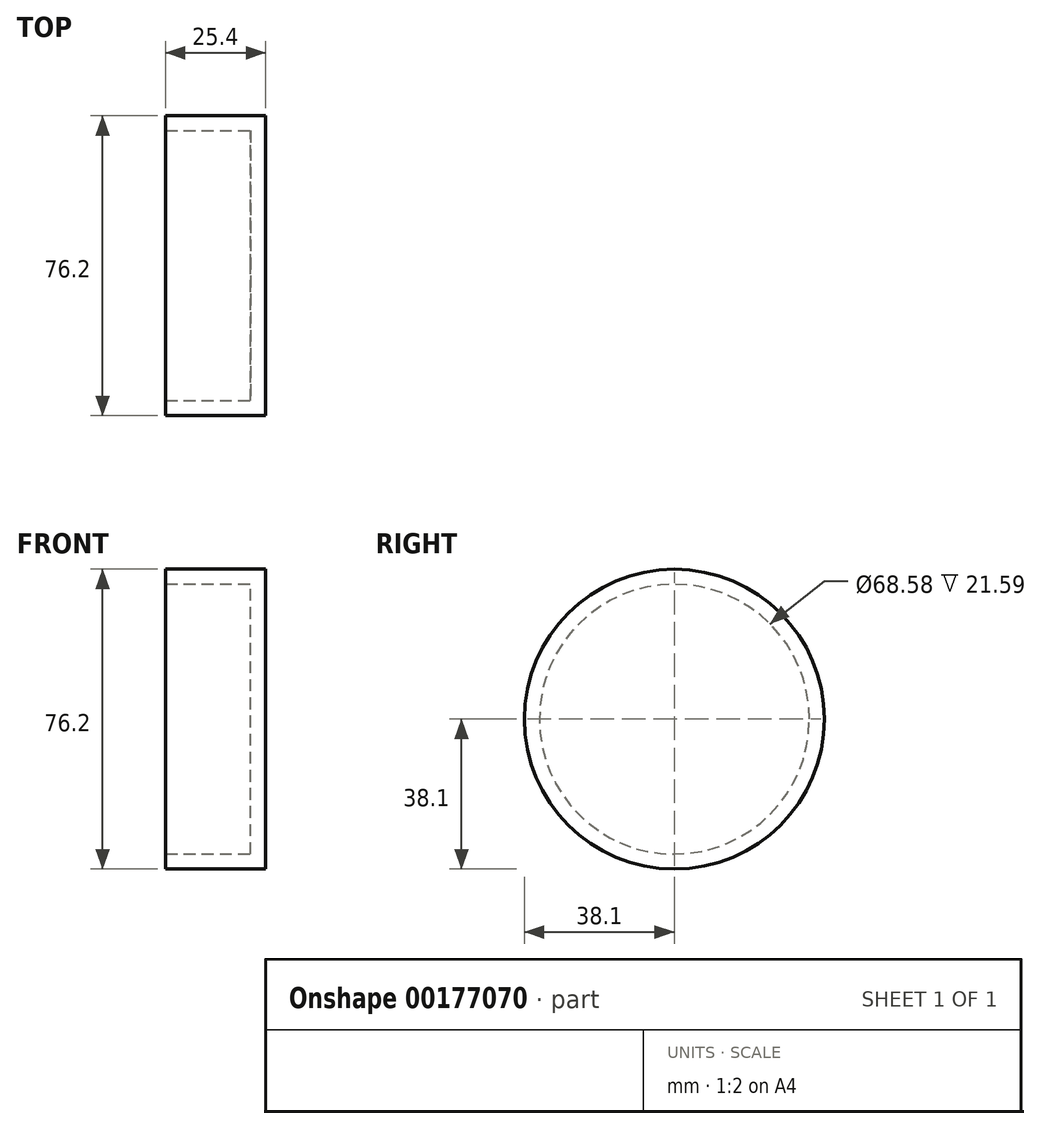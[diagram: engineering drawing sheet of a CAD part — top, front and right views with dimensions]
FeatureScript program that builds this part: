
annotation { "Feature Type Name" : "Feature", "Feature Type Description" : "" }
export const myFeature = defineFeature(function(context is Context, id is Id, definition is map)
    precondition{}
    {
        {
            var Q0;
            Q0=qCreatedBy(makeId("Right.planeOp"),FACE);
            var sketch = newSketch(context, id + "F0", { "sketchPlane" : qUnion([Q0])});
            skCircle(sketch, "E0", {"center": v(0, 0) * mm, "radius": 38.1 * mm});
            skSolve(sketch);
        }
        {
            var Q0;
            Q0=makeQuery(id+"F0.imprint","IMPRINT",FACE,{"disambiguationData":[TD([[makeQuery(id+"F0.imprint","IMPRINT",EDGE,{"derivedFrom":sQuery(id+"F0.wireOp",EDGE,"E0")}),1.0]])]});
            extrude(context, id + "F1", {"entities" : qUnion([Q0]), "oppositeDirection" : true, "depth" : 25.4 * mm});
        }
        {
            var Q0;
            Q0=makeQuery(id+"F1.opExtrude","CAP_FACE",FACE,{"disambiguationData":[OSD([sQuery(id+"F0.wireOp",EDGE,"E0")])],"isStart":false});
            shell(context, id + "F2", {"entities" : qUnion([Q0]), "thickness" : 3.8 * mm});
        }
    });
